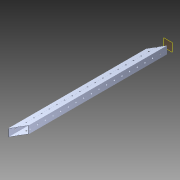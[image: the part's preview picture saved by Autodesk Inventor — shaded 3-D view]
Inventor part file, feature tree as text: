
AUTODESK INVENTOR PART (.ipt)
format: ipt  version: 2014 SP1 (Build 180222100, 222)  size: 1,280,512 bytes
history: native  units: in
note: dims shown in document units (in); Inventor stores cm internally (conversion verified against a paired STEP export)
features: extrude x3, sketch x3, pattern_circular x1, other x1, plane x1, imported_body x1
ambient origin geometry x8: Origin, YZ Plane, XZ Plane, XY Plane, X Axis, Y Axis, Z Axis, Center Point
bodies: Body1 (feature_tree)
feature tree (10):
  pattern_circular  "CirPattern2"
  other  "217-3426-STEP1"
  plane  "Work Plane1"
  extrude  "Extrusion1"  Depth=3937.0079in TaperAngle=0.0deg
  extrude  "Extrusion3"  Depth=3.937in TaperAngle=0.0deg
  extrude  "Extrusion4"  [1 undecoded]
  imported_body  "Base1"
  sketch  "Sketch1"  dims[d0=-21.0in d1=3937.0079in d2=0.0in]
  sketch  "Sketch4"  dims[d5=3.937in d6=0.0in d7=3.937in d8=0.0in]
  sketch  "Sketch5"
note: 1 required parameter value undecoded (feature->parameter linkage not recoverable at this tier; creation-order binding heuristic only, values carry confidence <= 0.55)
